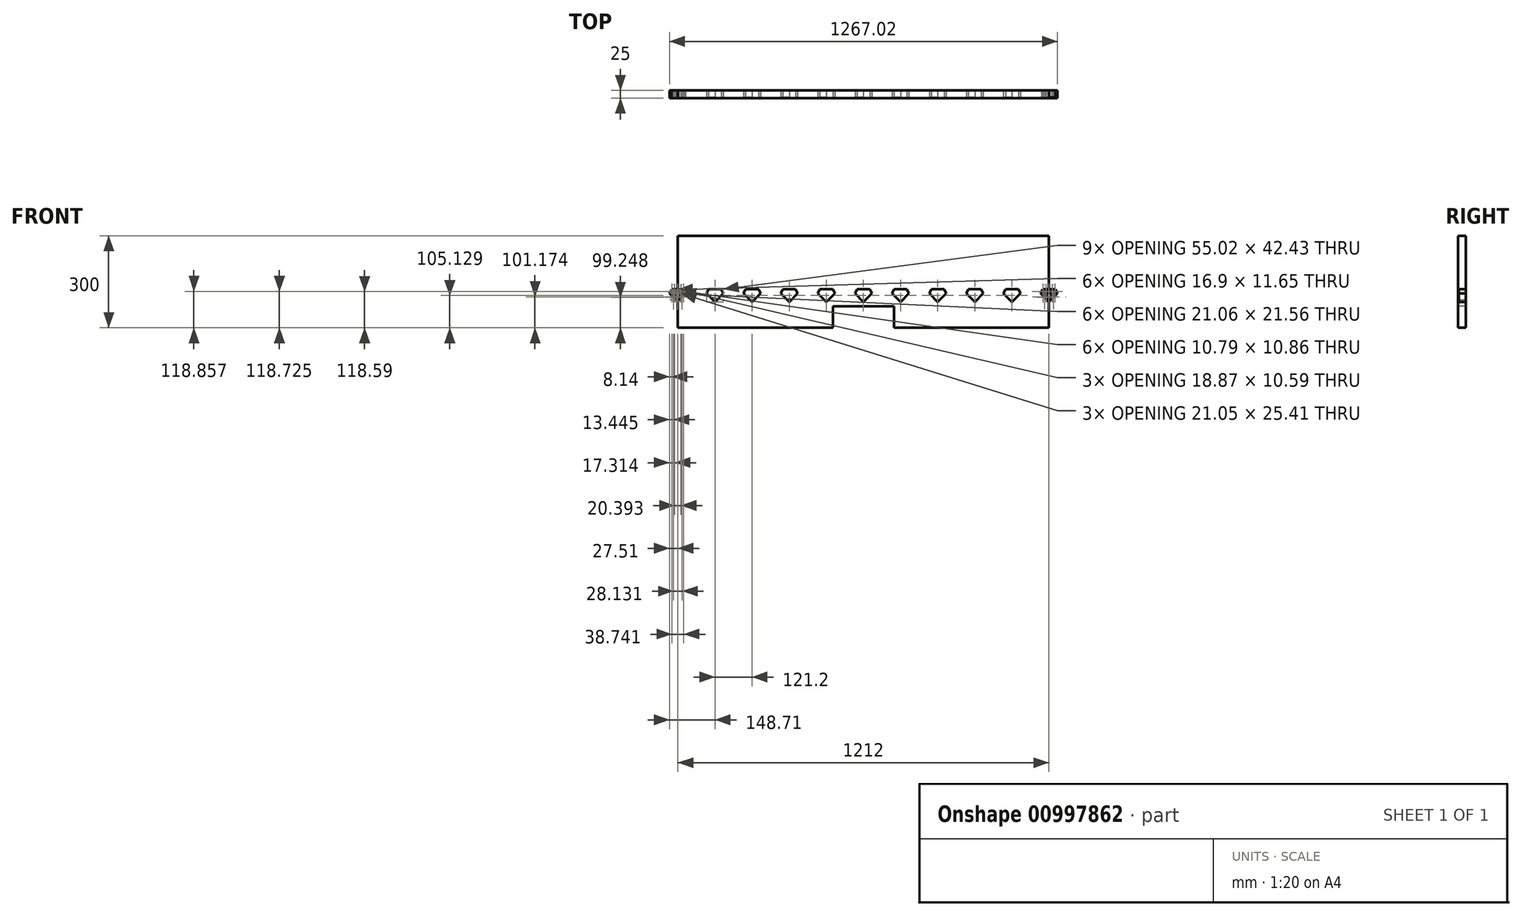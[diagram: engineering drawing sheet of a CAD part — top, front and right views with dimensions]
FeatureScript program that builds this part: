
annotation { "Feature Type Name" : "Feature", "Feature Type Description" : "" }
export const myFeature = defineFeature(function(context is Context, id is Id, definition is map)
    precondition{}
    {
        {
            var Q0;
            Q0=qCreatedBy(makeId("Front.planeOp"),FACE);
            var sketch = newSketch(context, id + "F0", { "sketchPlane" : qUnion([Q0])});
            skLineSegment(sketch, "E0.bottom", {"start": v(0, 0) * mm, "end": v(-506, 0) * mm});
            skLineSegment(sketch, "E0.top", {"start": v(0, 300) * mm, "end": v(-1212, 300) * mm});
            skLineSegment(sketch, "E0.left", {"start": v(0, 0) * mm, "end": v(0, 84.57) * mm});
            skLineSegment(sketch, "E0.right", {"start": v(-1212, 0) * mm, "end": v(-1212, 83.91) * mm});
            skLineSegment(sketch, "E1", {"start": v(-506, 0) * mm, "end": v(-506, 70) * mm});
            skLineSegment(sketch, "E2", {"start": v(-506, 70) * mm, "end": v(-706, 70) * mm});
            skLineSegment(sketch, "E3", {"start": v(-706, 70) * mm, "end": v(-706, 0) * mm});
            skPoint(sketch, "E4.orphan", {"position": v(-606, 0) * mm});
            skLineSegment(sketch, "E5.trimOffspring", {"start": v(-706, 0) * mm, "end": v(-1212, 0) * mm});
            skLineSegment(sketch, "E6.trimOffspring", {"start": v(0, 139.59) * mm, "end": v(0, 300) * mm});
            skLineSegment(sketch, "E7.trimOffspring", {"start": v(-1212, 139.59) * mm, "end": v(-1212, 300) * mm});
            skPoint(sketch, "E8.endSnap0", {"position": v(-1209.04, 125.07) * mm});
            skPoint(sketch, "E9.end.orphan", {"position": v(-1239.5, 112.08) * mm});
            skPoint(sketch, "E9.start.orphan", {"position": v(-1225.95, 125.07) * mm});
            skPoint(sketch, "E10.0.midPoint", {"position": v(-1195.54, 115.82) * mm});
            skLineSegment(sketch, "E11", {"start": v(-1212, 123.88) * mm, "end": v(-1202.56, 113.3) * mm});
            skLineSegment(sketch, "E12", {"start": v(-1202.56, 113.3) * mm, "end": v(-1212, 113.3) * mm});
            skLineSegment(sketch, "E13", {"start": v(-1212, 86.54) * mm, "end": v(-1201.48, 111.96) * mm});
            skLineSegment(sketch, "E14", {"start": v(-1201.48, 111.96) * mm, "end": v(-1212, 111.96) * mm});
            skLineSegment(sketch, "E15", {"start": v(-1199.56, 111.96) * mm, "end": v(-1208.46, 90.4) * mm});
            skLineSegment(sketch, "E16", {"start": v(-1208.46, 90.4) * mm, "end": v(-1187.4, 111.96) * mm});
            skLineSegment(sketch, "E17", {"start": v(-1187.4, 111.96) * mm, "end": v(-1199.56, 111.96) * mm});
            skLineSegment(sketch, "E18", {"start": v(-1198.03, 113.3) * mm, "end": v(-1187.23, 113.3) * mm});
            skLineSegment(sketch, "E19", {"start": v(-1187.23, 113.3) * mm, "end": v(-1192.13, 124.16) * mm});
            skLineSegment(sketch, "E20", {"start": v(-1192.13, 124.16) * mm, "end": v(-1198.03, 113.3) * mm});
            skLineSegment(sketch, "E21", {"start": v(-1210.25, 124.68) * mm, "end": v(-1199.87, 113.03) * mm});
            skLineSegment(sketch, "E22", {"start": v(-1199.87, 113.03) * mm, "end": v(-1193.35, 124.68) * mm});
            skLineSegment(sketch, "E23", {"start": v(-1193.35, 124.68) * mm, "end": v(-1210.25, 124.68) * mm});
            skLineSegment(sketch, "E24", {"start": v(-1212, 123.88) * mm, "end": v(-1212, 83.91) * mm});
            skPoint(sketch, "E25.end.orphan", {"position": v(-1192.13, 125.07) * mm});
            skLineSegment(sketch, "E26.trimOffspring", {"start": v(-1184.5, 112.08) * mm, "end": v(-1090.8, 112.08) * mm, "construction": true});
            skPoint(sketch, "E27.end.orphan", {"position": v(-1199.5, 112.08) * mm});
            skPoint(sketch, "E28.orphan", {"position": v(-1212, 125.07) * mm});
            skLineSegment(sketch, "E29.MirrorCS", {"start": v(-1230.65, 124.68) * mm, "end": v(-1213.75, 124.68) * mm});
            skLineSegment(sketch, "E30.MirrorCS", {"start": v(-1213.75, 124.68) * mm, "end": v(-1224.13, 113.03) * mm});
            skLineSegment(sketch, "E31.MirrorCS", {"start": v(-1212, 123.88) * mm, "end": v(-1221.44, 113.3) * mm});
            skLineSegment(sketch, "E32.MirrorCS", {"start": v(-1231.87, 124.16) * mm, "end": v(-1225.97, 113.3) * mm});
            skLineSegment(sketch, "E33.MirrorCS", {"start": v(-1236.77, 113.3) * mm, "end": v(-1231.87, 124.16) * mm});
            skLineSegment(sketch, "E34.MirrorCS", {"start": v(-1225.97, 113.3) * mm, "end": v(-1236.77, 113.3) * mm});
            skLineSegment(sketch, "E35.MirrorCS", {"start": v(-1236.6, 111.96) * mm, "end": v(-1224.44, 111.96) * mm});
            skLineSegment(sketch, "E36.MirrorCS", {"start": v(-1215.54, 90.4) * mm, "end": v(-1236.6, 111.96) * mm});
            skLineSegment(sketch, "E37.MirrorCS", {"start": v(-1224.44, 111.96) * mm, "end": v(-1215.54, 90.4) * mm});
            skLineSegment(sketch, "E38.MirrorCS", {"start": v(-1212, 86.54) * mm, "end": v(-1222.52, 111.96) * mm});
            skLineSegment(sketch, "E39.MirrorCS", {"start": v(-1222.52, 111.96) * mm, "end": v(-1212, 111.96) * mm});
            skLineSegment(sketch, "E40.MirrorCS", {"start": v(-1221.44, 113.3) * mm, "end": v(-1212, 113.3) * mm});
            skLineSegment(sketch, "E41.MirrorCS", {"start": v(-1224.13, 113.03) * mm, "end": v(-1230.65, 124.68) * mm});
            skLineSegment(sketch, "E42", {"start": v(-1212, 83.91) * mm, "end": v(-1184.5, 112.08) * mm});
            skLineSegment(sketch, "E43", {"start": v(-1184.5, 112.08) * mm, "end": v(-1190.92, 126.35) * mm});
            skLineSegment(sketch, "E44", {"start": v(-1212, 139.59) * mm, "end": v(-1212, 126.35) * mm});
            skLineSegment(sketch, "E45", {"start": v(-1212, 126.35) * mm, "end": v(-1190.92, 126.35) * mm});
            skPoint(sketch, "E46.center.orphan", {"position": v(-1212, 112.08) * mm});
            skLineSegment(sketch, "E47.MirrorCS", {"start": v(-1212, 126.35) * mm, "end": v(-1233.08, 126.35) * mm});
            skLineSegment(sketch, "E48.MirrorCS", {"start": v(-1239.5, 112.08) * mm, "end": v(-1233.08, 126.35) * mm});
            skLineSegment(sketch, "E49.MirrorCS", {"start": v(-1212, 83.91) * mm, "end": v(-1239.5, 112.08) * mm});
            skLineSegment(sketch, "E50.1.0.0", {"start": v(-1090.8, 126.35) * mm, "end": v(-1069.72, 126.35) * mm});
            skLineSegment(sketch, "E50.1.0.1", {"start": v(-1090.8, 126.35) * mm, "end": v(-1111.88, 126.35) * mm});
            skLineSegment(sketch, "E50.1.0.2", {"start": v(-1090.8, 123.88) * mm, "end": v(-1100.24, 113.3) * mm});
            skLineSegment(sketch, "E50.1.0.3", {"start": v(-1092.55, 124.68) * mm, "end": v(-1102.93, 113.03) * mm});
            skLineSegment(sketch, "E50.1.0.4", {"start": v(-1109.45, 124.68) * mm, "end": v(-1092.55, 124.68) * mm});
            skLineSegment(sketch, "E50.1.0.5", {"start": v(-1090.8, 123.88) * mm, "end": v(-1081.36, 113.3) * mm});
            skLineSegment(sketch, "E50.1.0.6", {"start": v(-1089.05, 124.68) * mm, "end": v(-1078.67, 113.03) * mm});
            skLineSegment(sketch, "E50.1.0.7", {"start": v(-1072.15, 124.68) * mm, "end": v(-1089.05, 124.68) * mm});
            skLineSegment(sketch, "E50.1.0.8", {"start": v(-1078.67, 113.03) * mm, "end": v(-1072.15, 124.68) * mm});
            skLineSegment(sketch, "E50.1.0.9", {"start": v(-1070.93, 124.16) * mm, "end": v(-1076.83, 113.3) * mm});
            skLineSegment(sketch, "E50.1.0.10", {"start": v(-1066.03, 113.3) * mm, "end": v(-1070.93, 124.16) * mm});
            skLineSegment(sketch, "E50.1.0.11", {"start": v(-1063.3, 112.08) * mm, "end": v(-1069.72, 126.35) * mm});
            skLineSegment(sketch, "E50.1.0.12", {"start": v(-1090.8, 83.91) * mm, "end": v(-1063.3, 112.08) * mm});
            skLineSegment(sketch, "E50.1.0.13", {"start": v(-1087.26, 90.4) * mm, "end": v(-1066.2, 111.96) * mm});
            skLineSegment(sketch, "E50.1.0.14", {"start": v(-1078.36, 111.96) * mm, "end": v(-1087.26, 90.4) * mm});
            skLineSegment(sketch, "E50.1.0.15", {"start": v(-1066.2, 111.96) * mm, "end": v(-1078.36, 111.96) * mm});
            skLineSegment(sketch, "E50.1.0.16", {"start": v(-1090.8, 86.54) * mm, "end": v(-1080.28, 111.96) * mm});
            skLineSegment(sketch, "E50.1.0.17", {"start": v(-1080.28, 111.96) * mm, "end": v(-1090.8, 111.96) * mm});
            skLineSegment(sketch, "E50.1.0.18", {"start": v(-1101.32, 111.96) * mm, "end": v(-1090.8, 111.96) * mm});
            skLineSegment(sketch, "E50.1.0.19", {"start": v(-1100.24, 113.3) * mm, "end": v(-1090.8, 113.3) * mm});
            skLineSegment(sketch, "E50.1.0.20", {"start": v(-1081.36, 113.3) * mm, "end": v(-1090.8, 113.3) * mm});
            skLineSegment(sketch, "E50.1.0.21", {"start": v(-1090.8, 86.54) * mm, "end": v(-1101.32, 111.96) * mm});
            skLineSegment(sketch, "E50.1.0.22", {"start": v(-1103.24, 111.96) * mm, "end": v(-1094.34, 90.4) * mm});
            skLineSegment(sketch, "E50.1.0.23", {"start": v(-1104.77, 113.3) * mm, "end": v(-1115.57, 113.3) * mm});
            skLineSegment(sketch, "E50.1.0.24", {"start": v(-1110.67, 124.16) * mm, "end": v(-1104.77, 113.3) * mm});
            skLineSegment(sketch, "E50.1.0.25", {"start": v(-1102.93, 113.03) * mm, "end": v(-1109.45, 124.68) * mm});
            skLineSegment(sketch, "E50.1.0.26", {"start": v(-1115.57, 113.3) * mm, "end": v(-1110.67, 124.16) * mm});
            skLineSegment(sketch, "E50.1.0.27", {"start": v(-1115.4, 111.96) * mm, "end": v(-1103.24, 111.96) * mm});
            skLineSegment(sketch, "E50.1.0.28", {"start": v(-1094.34, 90.4) * mm, "end": v(-1115.4, 111.96) * mm});
            skLineSegment(sketch, "E50.1.0.29", {"start": v(-1090.8, 83.91) * mm, "end": v(-1118.3, 112.08) * mm});
            skLineSegment(sketch, "E50.1.0.30", {"start": v(-1118.3, 112.08) * mm, "end": v(-1111.88, 126.35) * mm});
            skLineSegment(sketch, "E50.2.0.0", {"start": v(-969.6, 126.35) * mm, "end": v(-948.52, 126.35) * mm});
            skLineSegment(sketch, "E50.2.0.1", {"start": v(-969.6, 126.35) * mm, "end": v(-990.68, 126.35) * mm});
            skLineSegment(sketch, "E50.2.0.2", {"start": v(-969.6, 123.88) * mm, "end": v(-979.04, 113.3) * mm});
            skLineSegment(sketch, "E50.2.0.3", {"start": v(-971.35, 124.68) * mm, "end": v(-981.73, 113.03) * mm});
            skLineSegment(sketch, "E50.2.0.4", {"start": v(-988.25, 124.68) * mm, "end": v(-971.35, 124.68) * mm});
            skLineSegment(sketch, "E50.2.0.5", {"start": v(-969.6, 123.88) * mm, "end": v(-960.16, 113.3) * mm});
            skLineSegment(sketch, "E50.2.0.6", {"start": v(-967.85, 124.68) * mm, "end": v(-957.47, 113.03) * mm});
            skLineSegment(sketch, "E50.2.0.7", {"start": v(-950.95, 124.68) * mm, "end": v(-967.85, 124.68) * mm});
            skLineSegment(sketch, "E50.2.0.8", {"start": v(-957.47, 113.03) * mm, "end": v(-950.95, 124.68) * mm});
            skLineSegment(sketch, "E50.2.0.9", {"start": v(-949.73, 124.16) * mm, "end": v(-955.63, 113.3) * mm});
            skLineSegment(sketch, "E50.2.0.10", {"start": v(-944.83, 113.3) * mm, "end": v(-949.73, 124.16) * mm});
            skLineSegment(sketch, "E50.2.0.11", {"start": v(-942.1, 112.08) * mm, "end": v(-948.52, 126.35) * mm});
            skLineSegment(sketch, "E50.2.0.12", {"start": v(-969.6, 83.91) * mm, "end": v(-942.1, 112.08) * mm});
            skLineSegment(sketch, "E50.2.0.13", {"start": v(-966.06, 90.4) * mm, "end": v(-945, 111.96) * mm});
            skLineSegment(sketch, "E50.2.0.14", {"start": v(-957.16, 111.96) * mm, "end": v(-966.06, 90.4) * mm});
            skLineSegment(sketch, "E50.2.0.15", {"start": v(-945, 111.96) * mm, "end": v(-957.16, 111.96) * mm});
            skLineSegment(sketch, "E50.2.0.16", {"start": v(-969.6, 86.54) * mm, "end": v(-959.08, 111.96) * mm});
            skLineSegment(sketch, "E50.2.0.17", {"start": v(-959.08, 111.96) * mm, "end": v(-969.6, 111.96) * mm});
            skLineSegment(sketch, "E50.2.0.18", {"start": v(-980.12, 111.96) * mm, "end": v(-969.6, 111.96) * mm});
            skLineSegment(sketch, "E50.2.0.19", {"start": v(-979.04, 113.3) * mm, "end": v(-969.6, 113.3) * mm});
            skLineSegment(sketch, "E50.2.0.20", {"start": v(-960.16, 113.3) * mm, "end": v(-969.6, 113.3) * mm});
            skLineSegment(sketch, "E50.2.0.21", {"start": v(-969.6, 86.54) * mm, "end": v(-980.12, 111.96) * mm});
            skLineSegment(sketch, "E50.2.0.22", {"start": v(-982.04, 111.96) * mm, "end": v(-973.14, 90.4) * mm});
            skLineSegment(sketch, "E50.2.0.23", {"start": v(-983.57, 113.3) * mm, "end": v(-994.37, 113.3) * mm});
            skLineSegment(sketch, "E50.2.0.24", {"start": v(-989.47, 124.16) * mm, "end": v(-983.57, 113.3) * mm});
            skLineSegment(sketch, "E50.2.0.25", {"start": v(-981.73, 113.03) * mm, "end": v(-988.25, 124.68) * mm});
            skLineSegment(sketch, "E50.2.0.26", {"start": v(-994.37, 113.3) * mm, "end": v(-989.47, 124.16) * mm});
            skLineSegment(sketch, "E50.2.0.27", {"start": v(-994.2, 111.96) * mm, "end": v(-982.04, 111.96) * mm});
            skLineSegment(sketch, "E50.2.0.28", {"start": v(-973.14, 90.4) * mm, "end": v(-994.2, 111.96) * mm});
            skLineSegment(sketch, "E50.2.0.29", {"start": v(-969.6, 83.91) * mm, "end": v(-997.1, 112.08) * mm});
            skLineSegment(sketch, "E50.2.0.30", {"start": v(-997.1, 112.08) * mm, "end": v(-990.68, 126.35) * mm});
            skLineSegment(sketch, "E50.3.0.0", {"start": v(-848.4, 126.35) * mm, "end": v(-827.32, 126.35) * mm});
            skLineSegment(sketch, "E50.3.0.1", {"start": v(-848.4, 126.35) * mm, "end": v(-869.48, 126.35) * mm});
            skLineSegment(sketch, "E50.3.0.2", {"start": v(-848.4, 123.88) * mm, "end": v(-857.84, 113.3) * mm});
            skLineSegment(sketch, "E50.3.0.3", {"start": v(-850.15, 124.68) * mm, "end": v(-860.53, 113.03) * mm});
            skLineSegment(sketch, "E50.3.0.4", {"start": v(-867.05, 124.68) * mm, "end": v(-850.15, 124.68) * mm});
            skLineSegment(sketch, "E50.3.0.5", {"start": v(-848.4, 123.88) * mm, "end": v(-838.96, 113.3) * mm});
            skLineSegment(sketch, "E50.3.0.6", {"start": v(-846.65, 124.68) * mm, "end": v(-836.27, 113.03) * mm});
            skLineSegment(sketch, "E50.3.0.7", {"start": v(-829.75, 124.68) * mm, "end": v(-846.65, 124.68) * mm});
            skLineSegment(sketch, "E50.3.0.8", {"start": v(-836.27, 113.03) * mm, "end": v(-829.75, 124.68) * mm});
            skLineSegment(sketch, "E50.3.0.9", {"start": v(-828.53, 124.16) * mm, "end": v(-834.43, 113.3) * mm});
            skLineSegment(sketch, "E50.3.0.10", {"start": v(-823.63, 113.3) * mm, "end": v(-828.53, 124.16) * mm});
            skLineSegment(sketch, "E50.3.0.11", {"start": v(-820.9, 112.08) * mm, "end": v(-827.32, 126.35) * mm});
            skLineSegment(sketch, "E50.3.0.12", {"start": v(-848.4, 83.91) * mm, "end": v(-820.9, 112.08) * mm});
            skLineSegment(sketch, "E50.3.0.13", {"start": v(-844.86, 90.4) * mm, "end": v(-823.8, 111.96) * mm});
            skLineSegment(sketch, "E50.3.0.14", {"start": v(-835.96, 111.96) * mm, "end": v(-844.86, 90.4) * mm});
            skLineSegment(sketch, "E50.3.0.15", {"start": v(-823.8, 111.96) * mm, "end": v(-835.96, 111.96) * mm});
            skLineSegment(sketch, "E50.3.0.16", {"start": v(-848.4, 86.54) * mm, "end": v(-837.88, 111.96) * mm});
            skLineSegment(sketch, "E50.3.0.17", {"start": v(-837.88, 111.96) * mm, "end": v(-848.4, 111.96) * mm});
            skLineSegment(sketch, "E50.3.0.18", {"start": v(-858.92, 111.96) * mm, "end": v(-848.4, 111.96) * mm});
            skLineSegment(sketch, "E50.3.0.19", {"start": v(-857.84, 113.3) * mm, "end": v(-848.4, 113.3) * mm});
            skLineSegment(sketch, "E50.3.0.20", {"start": v(-838.96, 113.3) * mm, "end": v(-848.4, 113.3) * mm});
            skLineSegment(sketch, "E50.3.0.21", {"start": v(-848.4, 86.54) * mm, "end": v(-858.92, 111.96) * mm});
            skLineSegment(sketch, "E50.3.0.22", {"start": v(-860.84, 111.96) * mm, "end": v(-851.94, 90.4) * mm});
            skLineSegment(sketch, "E50.3.0.23", {"start": v(-862.37, 113.3) * mm, "end": v(-873.17, 113.3) * mm});
            skLineSegment(sketch, "E50.3.0.24", {"start": v(-868.27, 124.16) * mm, "end": v(-862.37, 113.3) * mm});
            skLineSegment(sketch, "E50.3.0.25", {"start": v(-860.53, 113.03) * mm, "end": v(-867.05, 124.68) * mm});
            skLineSegment(sketch, "E50.3.0.26", {"start": v(-873.17, 113.3) * mm, "end": v(-868.27, 124.16) * mm});
            skLineSegment(sketch, "E50.3.0.27", {"start": v(-873, 111.96) * mm, "end": v(-860.84, 111.96) * mm});
            skLineSegment(sketch, "E50.3.0.28", {"start": v(-851.94, 90.4) * mm, "end": v(-873, 111.96) * mm});
            skLineSegment(sketch, "E50.3.0.29", {"start": v(-848.4, 83.91) * mm, "end": v(-875.9, 112.08) * mm});
            skLineSegment(sketch, "E50.3.0.30", {"start": v(-875.9, 112.08) * mm, "end": v(-869.48, 126.35) * mm});
            skLineSegment(sketch, "E50.4.0.0", {"start": v(-727.2, 126.35) * mm, "end": v(-706.12, 126.35) * mm});
            skLineSegment(sketch, "E50.4.0.1", {"start": v(-727.2, 126.35) * mm, "end": v(-748.28, 126.35) * mm});
            skLineSegment(sketch, "E50.4.0.2", {"start": v(-727.2, 123.88) * mm, "end": v(-736.64, 113.3) * mm});
            skLineSegment(sketch, "E50.4.0.3", {"start": v(-728.95, 124.68) * mm, "end": v(-739.33, 113.03) * mm});
            skLineSegment(sketch, "E50.4.0.4", {"start": v(-745.85, 124.68) * mm, "end": v(-728.95, 124.68) * mm});
            skLineSegment(sketch, "E50.4.0.5", {"start": v(-727.2, 123.88) * mm, "end": v(-717.76, 113.3) * mm});
            skLineSegment(sketch, "E50.4.0.6", {"start": v(-725.45, 124.68) * mm, "end": v(-715.07, 113.03) * mm});
            skLineSegment(sketch, "E50.4.0.7", {"start": v(-708.55, 124.68) * mm, "end": v(-725.45, 124.68) * mm});
            skLineSegment(sketch, "E50.4.0.8", {"start": v(-715.07, 113.03) * mm, "end": v(-708.55, 124.68) * mm});
            skLineSegment(sketch, "E50.4.0.9", {"start": v(-707.33, 124.16) * mm, "end": v(-713.23, 113.3) * mm});
            skLineSegment(sketch, "E50.4.0.10", {"start": v(-702.43, 113.3) * mm, "end": v(-707.33, 124.16) * mm});
            skLineSegment(sketch, "E50.4.0.11", {"start": v(-699.7, 112.08) * mm, "end": v(-706.12, 126.35) * mm});
            skLineSegment(sketch, "E50.4.0.12", {"start": v(-727.2, 83.91) * mm, "end": v(-699.7, 112.08) * mm});
            skLineSegment(sketch, "E50.4.0.13", {"start": v(-723.66, 90.4) * mm, "end": v(-702.6, 111.96) * mm});
            skLineSegment(sketch, "E50.4.0.14", {"start": v(-714.76, 111.96) * mm, "end": v(-723.66, 90.4) * mm});
            skLineSegment(sketch, "E50.4.0.15", {"start": v(-702.6, 111.96) * mm, "end": v(-714.76, 111.96) * mm});
            skLineSegment(sketch, "E50.4.0.16", {"start": v(-727.2, 86.54) * mm, "end": v(-716.68, 111.96) * mm});
            skLineSegment(sketch, "E50.4.0.17", {"start": v(-716.68, 111.96) * mm, "end": v(-727.2, 111.96) * mm});
            skLineSegment(sketch, "E50.4.0.18", {"start": v(-737.72, 111.96) * mm, "end": v(-727.2, 111.96) * mm});
            skLineSegment(sketch, "E50.4.0.19", {"start": v(-736.64, 113.3) * mm, "end": v(-727.2, 113.3) * mm});
            skLineSegment(sketch, "E50.4.0.20", {"start": v(-717.76, 113.3) * mm, "end": v(-727.2, 113.3) * mm});
            skLineSegment(sketch, "E50.4.0.21", {"start": v(-727.2, 86.54) * mm, "end": v(-737.72, 111.96) * mm});
            skLineSegment(sketch, "E50.4.0.22", {"start": v(-739.64, 111.96) * mm, "end": v(-730.74, 90.4) * mm});
            skLineSegment(sketch, "E50.4.0.23", {"start": v(-741.17, 113.3) * mm, "end": v(-751.97, 113.3) * mm});
            skLineSegment(sketch, "E50.4.0.24", {"start": v(-747.07, 124.16) * mm, "end": v(-741.17, 113.3) * mm});
            skLineSegment(sketch, "E50.4.0.25", {"start": v(-739.33, 113.03) * mm, "end": v(-745.85, 124.68) * mm});
            skLineSegment(sketch, "E50.4.0.26", {"start": v(-751.97, 113.3) * mm, "end": v(-747.07, 124.16) * mm});
            skLineSegment(sketch, "E50.4.0.27", {"start": v(-751.8, 111.96) * mm, "end": v(-739.64, 111.96) * mm});
            skLineSegment(sketch, "E50.4.0.28", {"start": v(-730.74, 90.4) * mm, "end": v(-751.8, 111.96) * mm});
            skLineSegment(sketch, "E50.4.0.29", {"start": v(-727.2, 83.91) * mm, "end": v(-754.7, 112.08) * mm});
            skLineSegment(sketch, "E50.4.0.30", {"start": v(-754.7, 112.08) * mm, "end": v(-748.28, 126.35) * mm});
            skLineSegment(sketch, "E50.5.0.0", {"start": v(-606, 126.35) * mm, "end": v(-584.92, 126.35) * mm});
            skLineSegment(sketch, "E50.5.0.1", {"start": v(-606, 126.35) * mm, "end": v(-627.08, 126.35) * mm});
            skLineSegment(sketch, "E50.5.0.2", {"start": v(-606, 123.88) * mm, "end": v(-615.44, 113.3) * mm});
            skLineSegment(sketch, "E50.5.0.3", {"start": v(-607.75, 124.68) * mm, "end": v(-618.13, 113.03) * mm});
            skLineSegment(sketch, "E50.5.0.4", {"start": v(-624.65, 124.68) * mm, "end": v(-607.75, 124.68) * mm});
            skLineSegment(sketch, "E50.5.0.5", {"start": v(-606, 123.88) * mm, "end": v(-596.56, 113.3) * mm});
            skLineSegment(sketch, "E50.5.0.6", {"start": v(-604.25, 124.68) * mm, "end": v(-593.87, 113.03) * mm});
            skLineSegment(sketch, "E50.5.0.7", {"start": v(-587.35, 124.68) * mm, "end": v(-604.25, 124.68) * mm});
            skLineSegment(sketch, "E50.5.0.8", {"start": v(-593.87, 113.03) * mm, "end": v(-587.35, 124.68) * mm});
            skLineSegment(sketch, "E50.5.0.9", {"start": v(-586.13, 124.16) * mm, "end": v(-592.03, 113.3) * mm});
            skLineSegment(sketch, "E50.5.0.10", {"start": v(-581.23, 113.3) * mm, "end": v(-586.13, 124.16) * mm});
            skLineSegment(sketch, "E50.5.0.11", {"start": v(-578.5, 112.08) * mm, "end": v(-584.92, 126.35) * mm});
            skLineSegment(sketch, "E50.5.0.12", {"start": v(-606, 83.91) * mm, "end": v(-578.5, 112.08) * mm});
            skLineSegment(sketch, "E50.5.0.13", {"start": v(-602.46, 90.4) * mm, "end": v(-581.4, 111.96) * mm});
            skLineSegment(sketch, "E50.5.0.14", {"start": v(-593.56, 111.96) * mm, "end": v(-602.46, 90.4) * mm});
            skLineSegment(sketch, "E50.5.0.15", {"start": v(-581.4, 111.96) * mm, "end": v(-593.56, 111.96) * mm});
            skLineSegment(sketch, "E50.5.0.16", {"start": v(-606, 86.54) * mm, "end": v(-595.48, 111.96) * mm});
            skLineSegment(sketch, "E50.5.0.17", {"start": v(-595.48, 111.96) * mm, "end": v(-606, 111.96) * mm});
            skLineSegment(sketch, "E50.5.0.18", {"start": v(-616.52, 111.96) * mm, "end": v(-606, 111.96) * mm});
            skLineSegment(sketch, "E50.5.0.19", {"start": v(-615.44, 113.3) * mm, "end": v(-606, 113.3) * mm});
            skLineSegment(sketch, "E50.5.0.20", {"start": v(-596.56, 113.3) * mm, "end": v(-606, 113.3) * mm});
            skLineSegment(sketch, "E50.5.0.21", {"start": v(-606, 86.54) * mm, "end": v(-616.52, 111.96) * mm});
            skLineSegment(sketch, "E50.5.0.22", {"start": v(-618.44, 111.96) * mm, "end": v(-609.54, 90.4) * mm});
            skLineSegment(sketch, "E50.5.0.23", {"start": v(-619.97, 113.3) * mm, "end": v(-630.77, 113.3) * mm});
            skLineSegment(sketch, "E50.5.0.24", {"start": v(-625.87, 124.16) * mm, "end": v(-619.97, 113.3) * mm});
            skLineSegment(sketch, "E50.5.0.25", {"start": v(-618.13, 113.03) * mm, "end": v(-624.65, 124.68) * mm});
            skLineSegment(sketch, "E50.5.0.26", {"start": v(-630.77, 113.3) * mm, "end": v(-625.87, 124.16) * mm});
            skLineSegment(sketch, "E50.5.0.27", {"start": v(-630.6, 111.96) * mm, "end": v(-618.44, 111.96) * mm});
            skLineSegment(sketch, "E50.5.0.28", {"start": v(-609.54, 90.4) * mm, "end": v(-630.6, 111.96) * mm});
            skLineSegment(sketch, "E50.5.0.29", {"start": v(-606, 83.91) * mm, "end": v(-633.5, 112.08) * mm});
            skLineSegment(sketch, "E50.5.0.30", {"start": v(-633.5, 112.08) * mm, "end": v(-627.08, 126.35) * mm});
            skLineSegment(sketch, "E50.6.0.0", {"start": v(-484.8, 126.35) * mm, "end": v(-463.72, 126.35) * mm});
            skLineSegment(sketch, "E50.6.0.1", {"start": v(-484.8, 126.35) * mm, "end": v(-505.88, 126.35) * mm});
            skLineSegment(sketch, "E50.6.0.2", {"start": v(-484.8, 123.88) * mm, "end": v(-494.24, 113.3) * mm});
            skLineSegment(sketch, "E50.6.0.3", {"start": v(-486.55, 124.68) * mm, "end": v(-496.93, 113.03) * mm});
            skLineSegment(sketch, "E50.6.0.4", {"start": v(-503.45, 124.68) * mm, "end": v(-486.55, 124.68) * mm});
            skLineSegment(sketch, "E50.6.0.5", {"start": v(-484.8, 123.88) * mm, "end": v(-475.36, 113.3) * mm});
            skLineSegment(sketch, "E50.6.0.6", {"start": v(-483.05, 124.68) * mm, "end": v(-472.67, 113.03) * mm});
            skLineSegment(sketch, "E50.6.0.7", {"start": v(-466.15, 124.68) * mm, "end": v(-483.05, 124.68) * mm});
            skLineSegment(sketch, "E50.6.0.8", {"start": v(-472.67, 113.03) * mm, "end": v(-466.15, 124.68) * mm});
            skLineSegment(sketch, "E50.6.0.9", {"start": v(-464.93, 124.16) * mm, "end": v(-470.83, 113.3) * mm});
            skLineSegment(sketch, "E50.6.0.10", {"start": v(-460.03, 113.3) * mm, "end": v(-464.93, 124.16) * mm});
            skLineSegment(sketch, "E50.6.0.11", {"start": v(-457.3, 112.08) * mm, "end": v(-463.72, 126.35) * mm});
            skLineSegment(sketch, "E50.6.0.12", {"start": v(-484.8, 83.91) * mm, "end": v(-457.3, 112.08) * mm});
            skLineSegment(sketch, "E50.6.0.13", {"start": v(-481.26, 90.4) * mm, "end": v(-460.2, 111.96) * mm});
            skLineSegment(sketch, "E50.6.0.14", {"start": v(-472.36, 111.96) * mm, "end": v(-481.26, 90.4) * mm});
            skLineSegment(sketch, "E50.6.0.15", {"start": v(-460.2, 111.96) * mm, "end": v(-472.36, 111.96) * mm});
            skLineSegment(sketch, "E50.6.0.16", {"start": v(-484.8, 86.54) * mm, "end": v(-474.28, 111.96) * mm});
            skLineSegment(sketch, "E50.6.0.17", {"start": v(-474.28, 111.96) * mm, "end": v(-484.8, 111.96) * mm});
            skLineSegment(sketch, "E50.6.0.18", {"start": v(-495.32, 111.96) * mm, "end": v(-484.8, 111.96) * mm});
            skLineSegment(sketch, "E50.6.0.19", {"start": v(-494.24, 113.3) * mm, "end": v(-484.8, 113.3) * mm});
            skLineSegment(sketch, "E50.6.0.20", {"start": v(-475.36, 113.3) * mm, "end": v(-484.8, 113.3) * mm});
            skLineSegment(sketch, "E50.6.0.21", {"start": v(-484.8, 86.54) * mm, "end": v(-495.32, 111.96) * mm});
            skLineSegment(sketch, "E50.6.0.22", {"start": v(-497.24, 111.96) * mm, "end": v(-488.34, 90.4) * mm});
            skLineSegment(sketch, "E50.6.0.23", {"start": v(-498.77, 113.3) * mm, "end": v(-509.57, 113.3) * mm});
            skLineSegment(sketch, "E50.6.0.24", {"start": v(-504.67, 124.16) * mm, "end": v(-498.77, 113.3) * mm});
            skLineSegment(sketch, "E50.6.0.25", {"start": v(-496.93, 113.03) * mm, "end": v(-503.45, 124.68) * mm});
            skLineSegment(sketch, "E50.6.0.26", {"start": v(-509.57, 113.3) * mm, "end": v(-504.67, 124.16) * mm});
            skLineSegment(sketch, "E50.6.0.27", {"start": v(-509.4, 111.96) * mm, "end": v(-497.24, 111.96) * mm});
            skLineSegment(sketch, "E50.6.0.28", {"start": v(-488.34, 90.4) * mm, "end": v(-509.4, 111.96) * mm});
            skLineSegment(sketch, "E50.6.0.29", {"start": v(-484.8, 83.91) * mm, "end": v(-512.3, 112.08) * mm});
            skLineSegment(sketch, "E50.6.0.30", {"start": v(-512.3, 112.08) * mm, "end": v(-505.88, 126.35) * mm});
            skLineSegment(sketch, "E50.7.0.0", {"start": v(-363.6, 126.35) * mm, "end": v(-342.52, 126.35) * mm});
            skLineSegment(sketch, "E50.7.0.1", {"start": v(-363.6, 126.35) * mm, "end": v(-384.68, 126.35) * mm});
            skLineSegment(sketch, "E50.7.0.2", {"start": v(-363.6, 123.88) * mm, "end": v(-373.04, 113.3) * mm});
            skLineSegment(sketch, "E50.7.0.3", {"start": v(-365.35, 124.68) * mm, "end": v(-375.73, 113.03) * mm});
            skLineSegment(sketch, "E50.7.0.4", {"start": v(-382.25, 124.68) * mm, "end": v(-365.35, 124.68) * mm});
            skLineSegment(sketch, "E50.7.0.5", {"start": v(-363.6, 123.88) * mm, "end": v(-354.16, 113.3) * mm});
            skLineSegment(sketch, "E50.7.0.6", {"start": v(-361.85, 124.68) * mm, "end": v(-351.47, 113.03) * mm});
            skLineSegment(sketch, "E50.7.0.7", {"start": v(-344.95, 124.68) * mm, "end": v(-361.85, 124.68) * mm});
            skLineSegment(sketch, "E50.7.0.8", {"start": v(-351.47, 113.03) * mm, "end": v(-344.95, 124.68) * mm});
            skLineSegment(sketch, "E50.7.0.9", {"start": v(-343.73, 124.16) * mm, "end": v(-349.63, 113.3) * mm});
            skLineSegment(sketch, "E50.7.0.10", {"start": v(-338.83, 113.3) * mm, "end": v(-343.73, 124.16) * mm});
            skLineSegment(sketch, "E50.7.0.11", {"start": v(-336.1, 112.08) * mm, "end": v(-342.52, 126.35) * mm});
            skLineSegment(sketch, "E50.7.0.12", {"start": v(-363.6, 83.91) * mm, "end": v(-336.1, 112.08) * mm});
            skLineSegment(sketch, "E50.7.0.13", {"start": v(-360.06, 90.4) * mm, "end": v(-339, 111.96) * mm});
            skLineSegment(sketch, "E50.7.0.14", {"start": v(-351.16, 111.96) * mm, "end": v(-360.06, 90.4) * mm});
            skLineSegment(sketch, "E50.7.0.15", {"start": v(-339, 111.96) * mm, "end": v(-351.16, 111.96) * mm});
            skLineSegment(sketch, "E50.7.0.16", {"start": v(-363.6, 86.54) * mm, "end": v(-353.08, 111.96) * mm});
            skLineSegment(sketch, "E50.7.0.17", {"start": v(-353.08, 111.96) * mm, "end": v(-363.6, 111.96) * mm});
            skLineSegment(sketch, "E50.7.0.18", {"start": v(-374.12, 111.96) * mm, "end": v(-363.6, 111.96) * mm});
            skLineSegment(sketch, "E50.7.0.19", {"start": v(-373.04, 113.3) * mm, "end": v(-363.6, 113.3) * mm});
            skLineSegment(sketch, "E50.7.0.20", {"start": v(-354.16, 113.3) * mm, "end": v(-363.6, 113.3) * mm});
            skLineSegment(sketch, "E50.7.0.21", {"start": v(-363.6, 86.54) * mm, "end": v(-374.12, 111.96) * mm});
            skLineSegment(sketch, "E50.7.0.22", {"start": v(-376.04, 111.96) * mm, "end": v(-367.14, 90.4) * mm});
            skLineSegment(sketch, "E50.7.0.23", {"start": v(-377.57, 113.3) * mm, "end": v(-388.37, 113.3) * mm});
            skLineSegment(sketch, "E50.7.0.24", {"start": v(-383.47, 124.16) * mm, "end": v(-377.57, 113.3) * mm});
            skLineSegment(sketch, "E50.7.0.25", {"start": v(-375.73, 113.03) * mm, "end": v(-382.25, 124.68) * mm});
            skLineSegment(sketch, "E50.7.0.26", {"start": v(-388.37, 113.3) * mm, "end": v(-383.47, 124.16) * mm});
            skLineSegment(sketch, "E50.7.0.27", {"start": v(-388.2, 111.96) * mm, "end": v(-376.04, 111.96) * mm});
            skLineSegment(sketch, "E50.7.0.28", {"start": v(-367.14, 90.4) * mm, "end": v(-388.2, 111.96) * mm});
            skLineSegment(sketch, "E50.7.0.29", {"start": v(-363.6, 83.91) * mm, "end": v(-391.1, 112.08) * mm});
            skLineSegment(sketch, "E50.7.0.30", {"start": v(-391.1, 112.08) * mm, "end": v(-384.68, 126.35) * mm});
            skLineSegment(sketch, "E50.8.0.0", {"start": v(-242.4, 126.35) * mm, "end": v(-221.32, 126.35) * mm});
            skLineSegment(sketch, "E50.8.0.1", {"start": v(-242.4, 126.35) * mm, "end": v(-263.48, 126.35) * mm});
            skLineSegment(sketch, "E50.8.0.2", {"start": v(-242.4, 123.88) * mm, "end": v(-251.84, 113.3) * mm});
            skLineSegment(sketch, "E50.8.0.3", {"start": v(-244.15, 124.68) * mm, "end": v(-254.53, 113.03) * mm});
            skLineSegment(sketch, "E50.8.0.4", {"start": v(-261.05, 124.68) * mm, "end": v(-244.15, 124.68) * mm});
            skLineSegment(sketch, "E50.8.0.5", {"start": v(-242.4, 123.88) * mm, "end": v(-232.96, 113.3) * mm});
            skLineSegment(sketch, "E50.8.0.6", {"start": v(-240.65, 124.68) * mm, "end": v(-230.27, 113.03) * mm});
            skLineSegment(sketch, "E50.8.0.7", {"start": v(-223.75, 124.68) * mm, "end": v(-240.65, 124.68) * mm});
            skLineSegment(sketch, "E50.8.0.8", {"start": v(-230.27, 113.03) * mm, "end": v(-223.75, 124.68) * mm});
            skLineSegment(sketch, "E50.8.0.9", {"start": v(-222.53, 124.16) * mm, "end": v(-228.43, 113.3) * mm});
            skLineSegment(sketch, "E50.8.0.10", {"start": v(-217.63, 113.3) * mm, "end": v(-222.53, 124.16) * mm});
            skLineSegment(sketch, "E50.8.0.11", {"start": v(-214.9, 112.08) * mm, "end": v(-221.32, 126.35) * mm});
            skLineSegment(sketch, "E50.8.0.12", {"start": v(-242.4, 83.91) * mm, "end": v(-214.9, 112.08) * mm});
            skLineSegment(sketch, "E50.8.0.13", {"start": v(-238.86, 90.4) * mm, "end": v(-217.8, 111.96) * mm});
            skLineSegment(sketch, "E50.8.0.14", {"start": v(-229.96, 111.96) * mm, "end": v(-238.86, 90.4) * mm});
            skLineSegment(sketch, "E50.8.0.15", {"start": v(-217.8, 111.96) * mm, "end": v(-229.96, 111.96) * mm});
            skLineSegment(sketch, "E50.8.0.16", {"start": v(-242.4, 86.54) * mm, "end": v(-231.88, 111.96) * mm});
            skLineSegment(sketch, "E50.8.0.17", {"start": v(-231.88, 111.96) * mm, "end": v(-242.4, 111.96) * mm});
            skLineSegment(sketch, "E50.8.0.18", {"start": v(-252.92, 111.96) * mm, "end": v(-242.4, 111.96) * mm});
            skLineSegment(sketch, "E50.8.0.19", {"start": v(-251.84, 113.3) * mm, "end": v(-242.4, 113.3) * mm});
            skLineSegment(sketch, "E50.8.0.20", {"start": v(-232.96, 113.3) * mm, "end": v(-242.4, 113.3) * mm});
            skLineSegment(sketch, "E50.8.0.21", {"start": v(-242.4, 86.54) * mm, "end": v(-252.92, 111.96) * mm});
            skLineSegment(sketch, "E50.8.0.22", {"start": v(-254.84, 111.96) * mm, "end": v(-245.94, 90.4) * mm});
            skLineSegment(sketch, "E50.8.0.23", {"start": v(-256.37, 113.3) * mm, "end": v(-267.17, 113.3) * mm});
            skLineSegment(sketch, "E50.8.0.24", {"start": v(-262.27, 124.16) * mm, "end": v(-256.37, 113.3) * mm});
            skLineSegment(sketch, "E50.8.0.25", {"start": v(-254.53, 113.03) * mm, "end": v(-261.05, 124.68) * mm});
            skLineSegment(sketch, "E50.8.0.26", {"start": v(-267.17, 113.3) * mm, "end": v(-262.27, 124.16) * mm});
            skLineSegment(sketch, "E50.8.0.27", {"start": v(-267, 111.96) * mm, "end": v(-254.84, 111.96) * mm});
            skLineSegment(sketch, "E50.8.0.28", {"start": v(-245.94, 90.4) * mm, "end": v(-267, 111.96) * mm});
            skLineSegment(sketch, "E50.8.0.29", {"start": v(-242.4, 83.91) * mm, "end": v(-269.9, 112.08) * mm});
            skLineSegment(sketch, "E50.8.0.30", {"start": v(-269.9, 112.08) * mm, "end": v(-263.48, 126.35) * mm});
            skLineSegment(sketch, "E50.9.0.0", {"start": v(-121.2, 126.35) * mm, "end": v(-100.12, 126.35) * mm});
            skLineSegment(sketch, "E50.9.0.1", {"start": v(-121.2, 126.35) * mm, "end": v(-142.28, 126.35) * mm});
            skLineSegment(sketch, "E50.9.0.2", {"start": v(-121.2, 123.88) * mm, "end": v(-130.64, 113.3) * mm});
            skLineSegment(sketch, "E50.9.0.3", {"start": v(-122.95, 124.68) * mm, "end": v(-133.33, 113.03) * mm});
            skLineSegment(sketch, "E50.9.0.4", {"start": v(-139.85, 124.68) * mm, "end": v(-122.95, 124.68) * mm});
            skLineSegment(sketch, "E50.9.0.5", {"start": v(-121.2, 123.88) * mm, "end": v(-111.76, 113.3) * mm});
            skLineSegment(sketch, "E50.9.0.6", {"start": v(-119.45, 124.68) * mm, "end": v(-109.07, 113.03) * mm});
            skLineSegment(sketch, "E50.9.0.7", {"start": v(-102.55, 124.68) * mm, "end": v(-119.45, 124.68) * mm});
            skLineSegment(sketch, "E50.9.0.8", {"start": v(-109.07, 113.03) * mm, "end": v(-102.55, 124.68) * mm});
            skLineSegment(sketch, "E50.9.0.9", {"start": v(-101.33, 124.16) * mm, "end": v(-107.23, 113.3) * mm});
            skLineSegment(sketch, "E50.9.0.10", {"start": v(-96.43, 113.3) * mm, "end": v(-101.33, 124.16) * mm});
            skLineSegment(sketch, "E50.9.0.11", {"start": v(-93.7, 112.08) * mm, "end": v(-100.12, 126.35) * mm});
            skLineSegment(sketch, "E50.9.0.12", {"start": v(-121.2, 83.91) * mm, "end": v(-93.7, 112.08) * mm});
            skLineSegment(sketch, "E50.9.0.13", {"start": v(-117.66, 90.4) * mm, "end": v(-96.6, 111.96) * mm});
            skLineSegment(sketch, "E50.9.0.14", {"start": v(-108.76, 111.96) * mm, "end": v(-117.66, 90.4) * mm});
            skLineSegment(sketch, "E50.9.0.15", {"start": v(-96.6, 111.96) * mm, "end": v(-108.76, 111.96) * mm});
            skLineSegment(sketch, "E50.9.0.16", {"start": v(-121.2, 86.54) * mm, "end": v(-110.68, 111.96) * mm});
            skLineSegment(sketch, "E50.9.0.17", {"start": v(-110.68, 111.96) * mm, "end": v(-121.2, 111.96) * mm});
            skLineSegment(sketch, "E50.9.0.18", {"start": v(-131.72, 111.96) * mm, "end": v(-121.2, 111.96) * mm});
            skLineSegment(sketch, "E50.9.0.19", {"start": v(-130.64, 113.3) * mm, "end": v(-121.2, 113.3) * mm});
            skLineSegment(sketch, "E50.9.0.20", {"start": v(-111.76, 113.3) * mm, "end": v(-121.2, 113.3) * mm});
            skLineSegment(sketch, "E50.9.0.21", {"start": v(-121.2, 86.54) * mm, "end": v(-131.72, 111.96) * mm});
            skLineSegment(sketch, "E50.9.0.22", {"start": v(-133.64, 111.96) * mm, "end": v(-124.74, 90.4) * mm});
            skLineSegment(sketch, "E50.9.0.23", {"start": v(-135.17, 113.3) * mm, "end": v(-145.97, 113.3) * mm});
            skLineSegment(sketch, "E50.9.0.24", {"start": v(-141.07, 124.16) * mm, "end": v(-135.17, 113.3) * mm});
            skLineSegment(sketch, "E50.9.0.25", {"start": v(-133.33, 113.03) * mm, "end": v(-139.85, 124.68) * mm});
            skLineSegment(sketch, "E50.9.0.26", {"start": v(-145.97, 113.3) * mm, "end": v(-141.07, 124.16) * mm});
            skLineSegment(sketch, "E50.9.0.27", {"start": v(-145.8, 111.96) * mm, "end": v(-133.64, 111.96) * mm});
            skLineSegment(sketch, "E50.9.0.28", {"start": v(-124.74, 90.4) * mm, "end": v(-145.8, 111.96) * mm});
            skLineSegment(sketch, "E50.9.0.29", {"start": v(-121.2, 83.91) * mm, "end": v(-148.7, 112.08) * mm});
            skLineSegment(sketch, "E50.9.0.30", {"start": v(-148.7, 112.08) * mm, "end": v(-142.28, 126.35) * mm});
            skLineSegment(sketch, "E50.10.0.0", {"start": v(0, 126.35) * mm, "end": v(21.08, 126.35) * mm});
            skLineSegment(sketch, "E50.10.0.1", {"start": v(0, 126.35) * mm, "end": v(-21.08, 126.35) * mm});
            skLineSegment(sketch, "E50.10.0.2", {"start": v(0, 123.88) * mm, "end": v(-9.44, 113.3) * mm});
            skLineSegment(sketch, "E50.10.0.3", {"start": v(-1.75, 124.68) * mm, "end": v(-12.13, 113.03) * mm});
            skLineSegment(sketch, "E50.10.0.4", {"start": v(-18.65, 124.68) * mm, "end": v(-1.75, 124.68) * mm});
            skLineSegment(sketch, "E50.10.0.5", {"start": v(0, 123.88) * mm, "end": v(9.44, 113.3) * mm});
            skLineSegment(sketch, "E50.10.0.6", {"start": v(1.75, 124.68) * mm, "end": v(12.13, 113.03) * mm});
            skLineSegment(sketch, "E50.10.0.7", {"start": v(18.65, 124.68) * mm, "end": v(1.75, 124.68) * mm});
            skLineSegment(sketch, "E50.10.0.8", {"start": v(12.13, 113.03) * mm, "end": v(18.65, 124.68) * mm});
            skLineSegment(sketch, "E50.10.0.9", {"start": v(19.87, 124.16) * mm, "end": v(13.97, 113.3) * mm});
            skLineSegment(sketch, "E50.10.0.10", {"start": v(24.77, 113.3) * mm, "end": v(19.87, 124.16) * mm});
            skLineSegment(sketch, "E50.10.0.11", {"start": v(27.5, 112.08) * mm, "end": v(21.08, 126.35) * mm});
            skLineSegment(sketch, "E50.10.0.12", {"start": v(0, 83.91) * mm, "end": v(27.5, 112.08) * mm});
            skLineSegment(sketch, "E50.10.0.13", {"start": v(3.54, 90.4) * mm, "end": v(24.6, 111.96) * mm});
            skLineSegment(sketch, "E50.10.0.14", {"start": v(12.44, 111.96) * mm, "end": v(3.54, 90.4) * mm});
            skLineSegment(sketch, "E50.10.0.15", {"start": v(24.6, 111.96) * mm, "end": v(12.44, 111.96) * mm});
            skLineSegment(sketch, "E50.10.0.16", {"start": v(0, 86.54) * mm, "end": v(10.52, 111.96) * mm});
            skLineSegment(sketch, "E50.10.0.17", {"start": v(10.52, 111.96) * mm, "end": v(0, 111.96) * mm});
            skLineSegment(sketch, "E50.10.0.18", {"start": v(-10.52, 111.96) * mm, "end": v(0, 111.96) * mm});
            skLineSegment(sketch, "E50.10.0.19", {"start": v(-9.44, 113.3) * mm, "end": v(0, 113.3) * mm});
            skLineSegment(sketch, "E50.10.0.20", {"start": v(9.44, 113.3) * mm, "end": v(0, 113.3) * mm});
            skLineSegment(sketch, "E50.10.0.21", {"start": v(0, 86.54) * mm, "end": v(-10.52, 111.96) * mm});
            skLineSegment(sketch, "E50.10.0.22", {"start": v(-12.44, 111.96) * mm, "end": v(-3.54, 90.4) * mm});
            skLineSegment(sketch, "E50.10.0.23", {"start": v(-13.97, 113.3) * mm, "end": v(-24.77, 113.3) * mm});
            skLineSegment(sketch, "E50.10.0.24", {"start": v(-19.87, 124.16) * mm, "end": v(-13.97, 113.3) * mm});
            skLineSegment(sketch, "E50.10.0.25", {"start": v(-12.13, 113.03) * mm, "end": v(-18.65, 124.68) * mm});
            skLineSegment(sketch, "E50.10.0.26", {"start": v(-24.77, 113.3) * mm, "end": v(-19.87, 124.16) * mm});
            skLineSegment(sketch, "E50.10.0.27", {"start": v(-24.6, 111.96) * mm, "end": v(-12.44, 111.96) * mm});
            skLineSegment(sketch, "E50.10.0.28", {"start": v(-3.54, 90.4) * mm, "end": v(-24.6, 111.96) * mm});
            skLineSegment(sketch, "E50.10.0.29", {"start": v(0, 83.91) * mm, "end": v(-27.5, 112.08) * mm});
            skLineSegment(sketch, "E50.10.0.30", {"start": v(-27.5, 112.08) * mm, "end": v(-21.08, 126.35) * mm});
            skLineSegment(sketch, "E50.direction1", {"start": v(-1212, 126.35) * mm, "end": v(-1090.8, 126.35) * mm, "construction": true});
            skLineSegment(sketch, "E51", {"start": v(0, 139.59) * mm, "end": v(0, 126.35) * mm});
            skLineSegment(sketch, "E52.1.0.0", {"start": v(-1076.83, 113.3) * mm, "end": v(-1066.03, 113.3) * mm});
            skLineSegment(sketch, "E52.2.0.0", {"start": v(-955.63, 113.3) * mm, "end": v(-944.83, 113.3) * mm});
            skLineSegment(sketch, "E52.direction1", {"start": v(-1198.03, 113.3) * mm, "end": v(-1076.83, 113.3) * mm, "construction": true});
            skLineSegment(sketch, "E53", {"start": v(-713.23, 113.3) * mm, "end": v(-702.43, 113.3) * mm, "construction": true});
            skLineSegment(sketch, "E54", {"start": v(-592.03, 113.3) * mm, "end": v(-581.23, 113.3) * mm, "construction": true});
            skLineSegment(sketch, "E55", {"start": v(-470.83, 113.3) * mm, "end": v(-460.03, 113.3) * mm, "construction": true});
            skLineSegment(sketch, "E56", {"start": v(-349.63, 113.3) * mm, "end": v(-338.83, 113.3) * mm, "construction": true});
            skLineSegment(sketch, "E57", {"start": v(-228.43, 113.3) * mm, "end": v(-217.63, 113.3) * mm, "construction": true});
            skLineSegment(sketch, "E58", {"start": v(-107.23, 113.3) * mm, "end": v(-96.43, 113.3) * mm, "construction": true});
            skLineSegment(sketch, "E59", {"start": v(13.97, 113.3) * mm, "end": v(24.77, 113.3) * mm});
            skSolve(sketch);
        }
        {
            var Q0;
            Q0=makeQuery(id+"F0.imprint","IMPRINT",FACE,{"disambiguationData":[TD([[makeQuery(id+"F0.imprint","IMPRINT",EDGE,{"derivedFrom":sQuery(id+"F0.wireOp",EDGE,"E0.top")}),1.0]])]});
            var sketch = newSketch(context, id + "F1", { "sketchPlane" : qUnion([Q0])});
            skText(sketch, "E60", { "text": "I want to make pizza", "fontName": "AllertaStencil-Regular.ttf"});
            const initialGuessF1  = {"E60": [-1.08442, 0.201, 1, 0, 0.06667]};
            skSetInitialGuess(sketch, initialGuessF1);
            skSolve(sketch);
        }
        {
            var Q0;
            Q0=makeQuery(id+"F1.imprint","IMPRINT",FACE,{"disambiguationData":[TD([[makeQuery(id+"F1.imprint","IMPRINT",EDGE,{"derivedFrom":makeQuery(id+"F0.imprint","IMPRINT",EDGE,{"derivedFrom":sQuery(id+"F0.wireOp",EDGE,"E50.1.0.0")})}),-1.0]])]});
            var Q1;
            Q1=makeQuery(id+"F1.imprint","IMPRINT",FACE,{"disambiguationData":[TD([[makeQuery(id+"F1.imprint","IMPRINT",EDGE,{"derivedFrom":makeQuery(id+"F0.imprint","IMPRINT",EDGE,{"derivedFrom":sQuery(id+"F0.wireOp",EDGE,"E50.2.0.0")})}),-1.0]])]});
            var Q2;
            Q2=makeQuery(id+"F1.imprint","IMPRINT",FACE,{"disambiguationData":[TD([[makeQuery(id+"F1.imprint","IMPRINT",EDGE,{"derivedFrom":makeQuery(id+"F0.imprint","IMPRINT",EDGE,{"derivedFrom":sQuery(id+"F0.wireOp",EDGE,"E50.3.0.0")})}),-1.0]])]});
            var Q3;
            Q3=makeQuery(id+"F1.imprint","IMPRINT",FACE,{"disambiguationData":[TD([[makeQuery(id+"F1.imprint","IMPRINT",EDGE,{"derivedFrom":makeQuery(id+"F0.imprint","IMPRINT",EDGE,{"derivedFrom":sQuery(id+"F0.wireOp",EDGE,"E50.4.0.0")})}),-1.0]])]});
            var Q4;
            Q4=makeQuery(id+"F1.imprint","IMPRINT",FACE,{"disambiguationData":[TD([[makeQuery(id+"F1.imprint","IMPRINT",EDGE,{"derivedFrom":makeQuery(id+"F0.imprint","IMPRINT",EDGE,{"derivedFrom":sQuery(id+"F0.wireOp",EDGE,"E50.5.0.0")})}),-1.0]])]});
            var Q5;
            Q5=makeQuery(id+"F1.imprint","IMPRINT",FACE,{"disambiguationData":[TD([[makeQuery(id+"F1.imprint","IMPRINT",EDGE,{"derivedFrom":makeQuery(id+"F0.imprint","IMPRINT",EDGE,{"derivedFrom":sQuery(id+"F0.wireOp",EDGE,"E50.6.0.0")})}),-1.0]])]});
            var Q6;
            Q6=makeQuery(id+"F1.imprint","IMPRINT",FACE,{"disambiguationData":[TD([[makeQuery(id+"F1.imprint","IMPRINT",EDGE,{"derivedFrom":makeQuery(id+"F0.imprint","IMPRINT",EDGE,{"derivedFrom":sQuery(id+"F0.wireOp",EDGE,"E50.7.0.0")})}),-1.0]])]});
            var Q7;
            Q7=makeQuery(id+"F1.imprint","IMPRINT",FACE,{"disambiguationData":[TD([[makeQuery(id+"F1.imprint","IMPRINT",EDGE,{"derivedFrom":makeQuery(id+"F0.imprint","IMPRINT",EDGE,{"derivedFrom":sQuery(id+"F0.wireOp",EDGE,"E50.8.0.0")})}),-1.0]])]});
            var Q8;
            Q8=makeQuery(id+"F1.imprint","IMPRINT",FACE,{"disambiguationData":[TD([[makeQuery(id+"F1.imprint","IMPRINT",EDGE,{"derivedFrom":makeQuery(id+"F0.imprint","IMPRINT",EDGE,{"derivedFrom":sQuery(id+"F0.wireOp",EDGE,"E50.9.0.0")})}),-1.0]])]});
            var Q9;
            Q9=makeQuery(id+"F0.imprint","IMPRINT",FACE,{"disambiguationData":[TD([[makeQuery(id+"F0.imprint","IMPRINT",EDGE,{"derivedFrom":sQuery(id+"F0.wireOp",EDGE,"E50.10.0.0")}),-1.0]])]});
            extrude(context, id + "F2", {"entities" : qUnion([Q0, Q1, Q2, Q3, Q4, Q5, Q6, Q7, Q8, Q9]), "oppositeDirection" : true, "depth" : 1.6 * mm, "offsetDistance" : 25 * mm});
        }
        {
            var Q0;
            Q0=makeQuery(id+"F1.imprint","IMPRINT",FACE,{"disambiguationData":[TD([[makeQuery(id+"F1.imprint","IMPRINT",EDGE,{"derivedFrom":sQuery(id+"F1.wireOp",EDGE,"E60.sketch_text.stroke-0")}),-1.0]])]});
            var Q1;
            Q1=makeQuery(id+"F1.imprint","IMPRINT",FACE,{"disambiguationData":[TD([[makeQuery(id+"F1.imprint","IMPRINT",EDGE,{"derivedFrom":sQuery(id+"F1.wireOp",EDGE,"E60.sketch_text.stroke-12")}),-1.0]])]});
            var Q2;
            Q2=makeQuery(id+"F1.imprint","IMPRINT",FACE,{"disambiguationData":[TD([[makeQuery(id+"F1.imprint","IMPRINT",EDGE,{"derivedFrom":sQuery(id+"F1.wireOp",EDGE,"E60.sketch_text.stroke-4")}),-1.0]])]});
            var Q3;
            Q3=makeQuery(id+"F1.imprint","IMPRINT",FACE,{"disambiguationData":[TD([[makeQuery(id+"F1.imprint","IMPRINT",EDGE,{"derivedFrom":sQuery(id+"F1.wireOp",EDGE,"E60.sketch_text.stroke-39")}),-1.0]])]});
            var Q4;
            Q4=makeQuery(id+"F1.imprint","IMPRINT",FACE,{"disambiguationData":[TD([[makeQuery(id+"F1.imprint","IMPRINT",EDGE,{"derivedFrom":sQuery(id+"F1.wireOp",EDGE,"E60.sketch_text.stroke-20")}),-1.0]])]});
            var Q5;
            Q5=makeQuery(id+"F1.imprint","IMPRINT",FACE,{"disambiguationData":[TD([[makeQuery(id+"F1.imprint","IMPRINT",EDGE,{"derivedFrom":sQuery(id+"F1.wireOp",EDGE,"E60.sketch_text.stroke-75")}),-1.0]])]});
            var Q6;
            Q6=makeQuery(id+"F1.imprint","IMPRINT",FACE,{"disambiguationData":[TD([[makeQuery(id+"F1.imprint","IMPRINT",EDGE,{"derivedFrom":sQuery(id+"F1.wireOp",EDGE,"E60.sketch_text.stroke-80")}),-1.0]])]});
            var Q7;
            Q7=makeQuery(id+"F1.imprint","IMPRINT",FACE,{"disambiguationData":[TD([[makeQuery(id+"F1.imprint","IMPRINT",EDGE,{"derivedFrom":sQuery(id+"F1.wireOp",EDGE,"E60.sketch_text.stroke-99")}),-1.0]])]});
            var Q8;
            Q8=makeQuery(id+"F1.imprint","IMPRINT",FACE,{"disambiguationData":[TD([[makeQuery(id+"F1.imprint","IMPRINT",EDGE,{"derivedFrom":sQuery(id+"F1.wireOp",EDGE,"E60.sketch_text.stroke-124")}),-1.0]])]});
            var Q9;
            Q9=makeQuery(id+"F1.imprint","IMPRINT",FACE,{"disambiguationData":[TD([[makeQuery(id+"F1.imprint","IMPRINT",EDGE,{"derivedFrom":sQuery(id+"F1.wireOp",EDGE,"E60.sketch_text.stroke-165")}),-1.0]])]});
            var Q10;
            Q10=makeQuery(id+"F1.imprint","IMPRINT",FACE,{"disambiguationData":[TD([[makeQuery(id+"F1.imprint","IMPRINT",EDGE,{"derivedFrom":sQuery(id+"F1.wireOp",EDGE,"E60.sketch_text.stroke-149")}),-1.0]])]});
            var Q11;
            Q11=makeQuery(id+"F1.imprint","IMPRINT",FACE,{"disambiguationData":[TD([[makeQuery(id+"F1.imprint","IMPRINT",EDGE,{"derivedFrom":sQuery(id+"F1.wireOp",EDGE,"E60.sketch_text.stroke-181")}),-1.0]])]});
            var Q12;
            Q12=makeQuery(id+"F1.imprint","IMPRINT",FACE,{"disambiguationData":[TD([[makeQuery(id+"F1.imprint","IMPRINT",EDGE,{"derivedFrom":sQuery(id+"F1.wireOp",EDGE,"E60.sketch_text.stroke-202")}),-1.0]])]});
            var Q13;
            Q13=makeQuery(id+"F1.imprint","IMPRINT",FACE,{"disambiguationData":[TD([[makeQuery(id+"F1.imprint","IMPRINT",EDGE,{"derivedFrom":sQuery(id+"F1.wireOp",EDGE,"E60.sketch_text.stroke-186")}),-1.0]])]});
            var Q14;
            Q14=makeQuery(id+"F1.imprint","IMPRINT",FACE,{"disambiguationData":[TD([[makeQuery(id+"F1.imprint","IMPRINT",EDGE,{"derivedFrom":sQuery(id+"F1.wireOp",EDGE,"E60.sketch_text.stroke-239")}),-1.0]])]});
            var Q15;
            Q15=makeQuery(id+"F1.imprint","IMPRINT",FACE,{"disambiguationData":[TD([[makeQuery(id+"F1.imprint","IMPRINT",EDGE,{"derivedFrom":sQuery(id+"F1.wireOp",EDGE,"E60.sketch_text.stroke-282")}),-1.0]])]});
            var Q16;
            Q16=makeQuery(id+"F1.imprint","IMPRINT",FACE,{"disambiguationData":[TD([[makeQuery(id+"F1.imprint","IMPRINT",EDGE,{"derivedFrom":sQuery(id+"F1.wireOp",EDGE,"E60.sketch_text.stroke-275")}),-1.0]])]});
            var Q17;
            Q17=makeQuery(id+"F1.imprint","IMPRINT",FACE,{"disambiguationData":[TD([[makeQuery(id+"F1.imprint","IMPRINT",EDGE,{"derivedFrom":sQuery(id+"F1.wireOp",EDGE,"E60.sketch_text.stroke-220")}),-1.0]])]});
            var Q18;
            Q18=makeQuery(id+"F1.imprint","IMPRINT",FACE,{"disambiguationData":[TD([[makeQuery(id+"F1.imprint","IMPRINT",EDGE,{"derivedFrom":sQuery(id+"F1.wireOp",EDGE,"E60.sketch_text.stroke-299")}),-1.0]])]});
            extrude(context, id + "F3", {"entities" : qUnion([Q0, Q1, Q2, Q3, Q4, Q5, Q6, Q7, Q8, Q9, Q10, Q11, Q12, Q13, Q14, Q15, Q16, Q17, Q18]), "operationType" : NewBodyOperationType.REMOVE, "depth" : 25 * mm, "offsetDistance" : 25 * mm});
        }
        {
            var Q0;
            Q0=makeQuery(id+"F1.imprint","IMPRINT",FACE,{"disambiguationData":[TD([[makeQuery(id+"F1.imprint","IMPRINT",EDGE,{"derivedFrom":sQuery(id+"F1.wireOp",EDGE,"E60.sketch_text.stroke-286")}),-1.0]])]});
            var Q1;
            Q1=makeQuery(id+"F1.imprint","IMPRINT",FACE,{"disambiguationData":[TD([[makeQuery(id+"F1.imprint","IMPRINT",EDGE,{"derivedFrom":sQuery(id+"F1.wireOp",EDGE,"E60.sketch_text.stroke-323")}),-1.0]])]});
            var Q2;
            Q2=makeQuery(id+"F1.imprint","IMPRINT",FACE,{"disambiguationData":[TD([[makeQuery(id+"F1.imprint","IMPRINT",EDGE,{"derivedFrom":sQuery(id+"F1.wireOp",EDGE,"E60.sketch_text.stroke-328")}),-1.0]])]});
            var Q3;
            Q3=makeQuery(id+"F1.imprint","IMPRINT",FACE,{"disambiguationData":[TD([[makeQuery(id+"F1.imprint","IMPRINT",EDGE,{"derivedFrom":sQuery(id+"F1.wireOp",EDGE,"E60.sketch_text.stroke-358")}),-1.0]])]});
            var Q4;
            Q4=makeQuery(id+"F1.imprint","IMPRINT",FACE,{"disambiguationData":[TD([[makeQuery(id+"F1.imprint","IMPRINT",EDGE,{"derivedFrom":sQuery(id+"F1.wireOp",EDGE,"E60.sketch_text.stroke-354")}),-1.0]])]});
            var Q5;
            Q5=makeQuery(id+"F1.imprint","IMPRINT",FACE,{"disambiguationData":[TD([[makeQuery(id+"F1.imprint","IMPRINT",EDGE,{"derivedFrom":sQuery(id+"F1.wireOp",EDGE,"E60.sketch_text.stroke-366")}),-1.0]])]});
            var Q6;
            Q6=makeQuery(id+"F1.imprint","IMPRINT",FACE,{"disambiguationData":[TD([[makeQuery(id+"F1.imprint","IMPRINT",EDGE,{"derivedFrom":sQuery(id+"F1.wireOp",EDGE,"E60.sketch_text.stroke-378")}),-1.0]])]});
            var Q7;
            Q7=makeQuery(id+"F1.imprint","IMPRINT",FACE,{"disambiguationData":[TD([[makeQuery(id+"F1.imprint","IMPRINT",EDGE,{"derivedFrom":sQuery(id+"F1.wireOp",EDGE,"E60.sketch_text.stroke-409")}),-1.0]])]});
            var Q8;
            Q8=makeQuery(id+"F1.imprint","IMPRINT",FACE,{"disambiguationData":[TD([[makeQuery(id+"F1.imprint","IMPRINT",EDGE,{"derivedFrom":sQuery(id+"F1.wireOp",EDGE,"E60.sketch_text.stroke-390")}),-1.0]])]});
            extrude(context, id + "F4", {"entities" : qUnion([Q0, Q1, Q2, Q3, Q4, Q5, Q6, Q7, Q8]), "operationType" : NewBodyOperationType.REMOVE, "depth" : 25 * mm, "offsetDistance" : 25 * mm});
        }
        {
            var Q0;
            Q0 = qSketchRegion(id + "F0", true);
            extrude(context, id + "F5", {"entities" : qUnion([Q0]), "oppositeDirection" : true, "depth" : 25 * mm, "offsetDistance" : 25 * mm});
        }
    });
